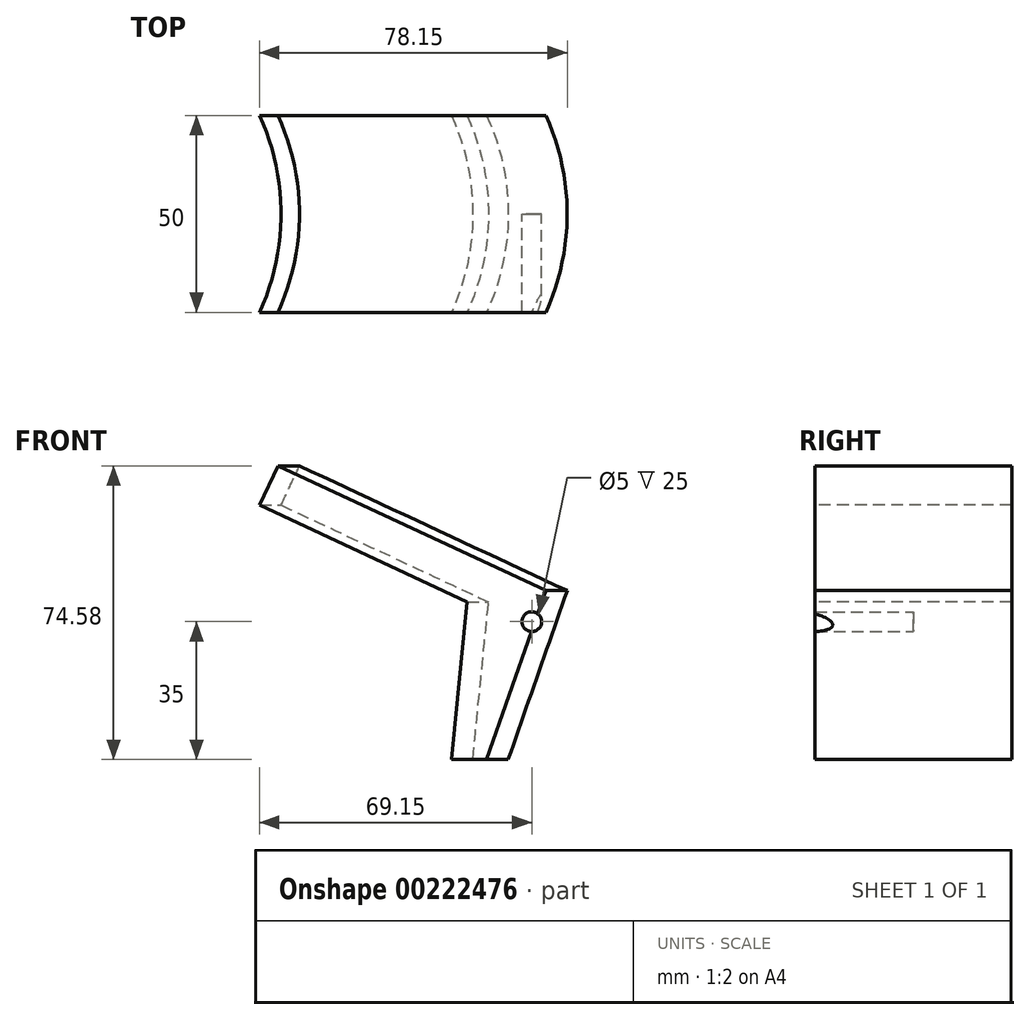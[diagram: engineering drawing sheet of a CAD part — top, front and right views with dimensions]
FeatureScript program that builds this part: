
annotation { "Feature Type Name" : "Feature", "Feature Type Description" : "" }
export const myFeature = defineFeature(function(context is Context, id is Id, definition is map)
    precondition{}
    {
        {
            var Q0;
            Q0=qCreatedBy(makeId("Front.planeOp"),FACE);
            var sketch = newSketch(context, id + "F0", { "sketchPlane" : qUnion([Q0])});
            skLineSegment(sketch, "E0", {"start": v(0, 0) * mm, "end": v(4, 40) * mm});
            skLineSegment(sketch, "E1", {"start": v(0, 0) * mm, "end": v(9, 0) * mm});
            skLineSegment(sketch, "E2", {"start": v(24, 42.86) * mm, "end": v(-44.03, 74.58) * mm});
            skLineSegment(sketch, "E3", {"start": v(4, 40) * mm, "end": v(-48.7, 64.57) * mm});
            skLineSegment(sketch, "E4", {"start": v(-60, 0) * mm, "end": v(-60, 154.93) * mm});
            skLineSegment(sketch, "E5", {"start": v(9, 0) * mm, "end": v(24, 42.86) * mm});
            skLineSegment(sketch, "E6", {"start": v(-48.7, 64.57) * mm, "end": v(-44.03, 74.58) * mm});
            skSolve(sketch);
        }
        {
            var Q0;
            Q0=qCreatedBy(makeId("Top.planeOp"),FACE);
            var sketch = newSketch(context, id + "F1", { "sketchPlane" : qUnion([Q0])});
            skArc(sketch, "E7", {"start": v(-5.46, 25) * mm, "mid": v(0, 0) * mm, "end": v(-5.46, -25) * mm});
            skPoint(sketch, "E8", {"position": v(0, 0) * mm});
            skSolve(sketch);
        }
        {
            var Q0;
            Q0=makeQuery(id+"F0.imprint","IMPRINT",FACE,{"disambiguationData":[TD([[makeQuery(id+"F0.imprint","IMPRINT",EDGE,{"derivedFrom":sQuery(id+"F0.wireOp",EDGE,"E0")}),-1.0]])]});
            var Q1;
            Q1=sQuery(id+"F1.wireOp",EDGE,"E7");
            sweep(context, id + "F2", {"profiles" : qUnion([Q0]), "path" : qUnion([Q1]), "keepProfileOrientation" : true});
        }
        {
            var Q0;
            Q0=qCreatedBy(makeId("Front.planeOp"),FACE);
            var sketch = newSketch(context, id + "F3", { "sketchPlane" : qUnion([Q0])});
            skCircle(sketch, "E9", {"center": v(15, 35) * mm, "radius": 2.5 * mm});
            skSolve(sketch);
        }
        {
            var Q0;
            Q0 = qSketchRegion(id + "F3", true);
            extrude(context, id + "F4", {"entities" : qUnion([Q0]), "operationType" : NewBodyOperationType.REMOVE, "depth" : 68.5 * mm});
        }
    });
